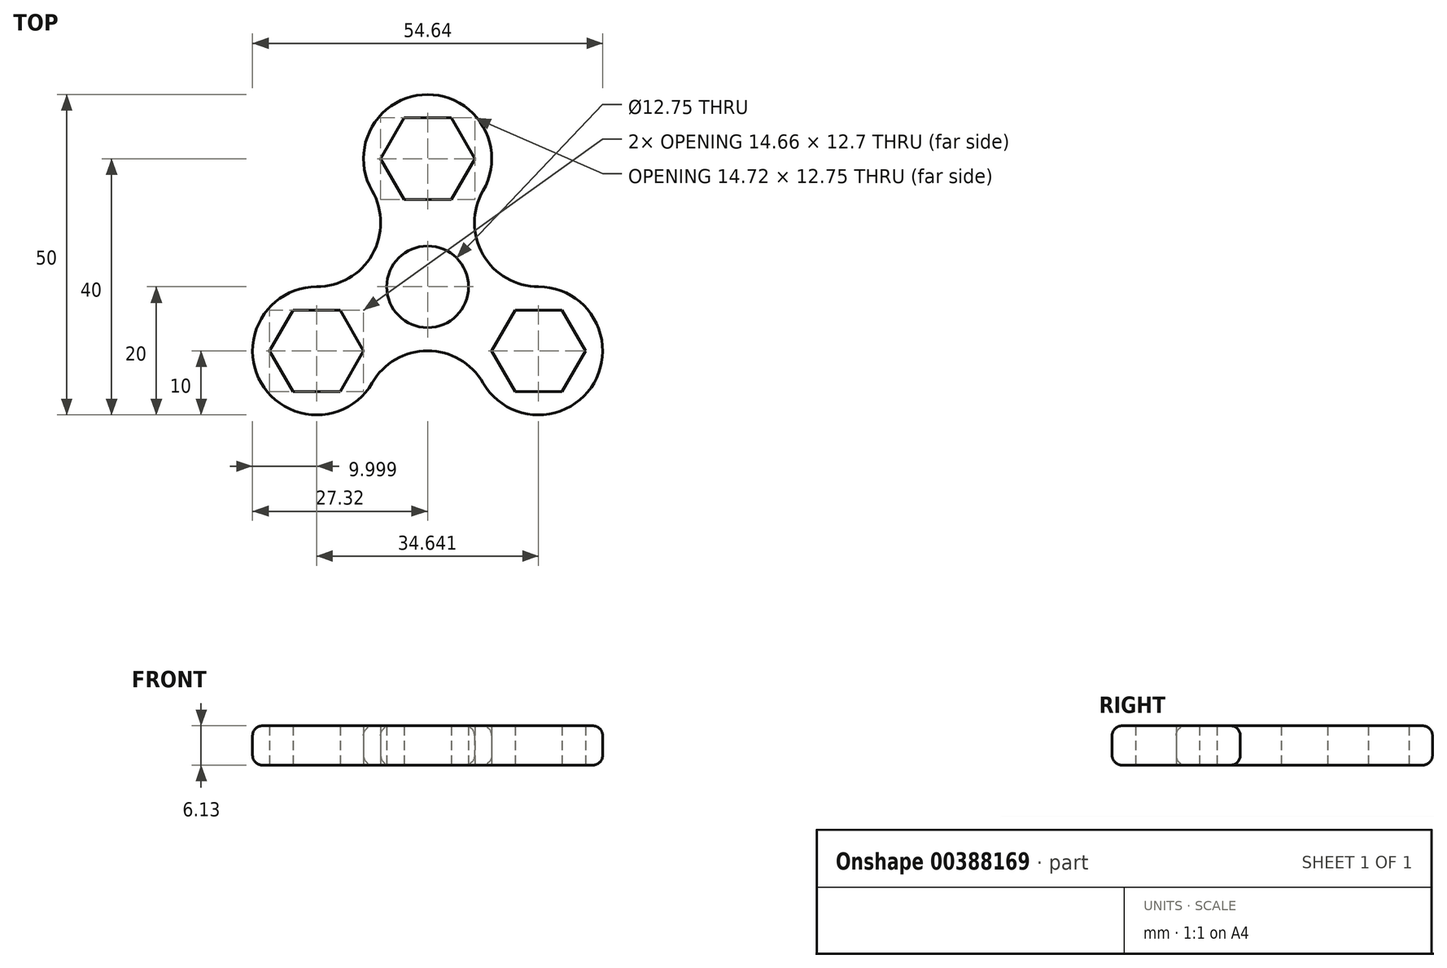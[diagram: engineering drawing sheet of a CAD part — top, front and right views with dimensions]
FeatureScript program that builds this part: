
annotation { "Feature Type Name" : "Feature", "Feature Type Description" : "" }
export const myFeature = defineFeature(function(context is Context, id is Id, definition is map)
    precondition{}
    {
        {
            var Q0;
            Q0=qCreatedBy(makeId("Top.planeOp"),FACE);
            var sketch = newSketch(context, id + "F0", { "sketchPlane" : qUnion([Q0])});
            skCircle(sketch, "E0", {"center": v(0, -20) * mm, "radius": 6.38 * mm});
            skLineSegment(sketch, "E1.0", {"start": v(-13.65, -23.65) * mm, "end": v(-9.99, -30) * mm});
            skLineSegment(sketch, "E1.1", {"start": v(-9.99, -30) * mm, "end": v(-13.65, -36.35) * mm});
            skLineSegment(sketch, "E1.2", {"start": v(-13.65, -36.35) * mm, "end": v(-20.99, -36.35) * mm});
            skLineSegment(sketch, "E1.3", {"start": v(-20.99, -36.35) * mm, "end": v(-24.65, -30) * mm});
            skLineSegment(sketch, "E1.4", {"start": v(-24.65, -30) * mm, "end": v(-20.99, -23.65) * mm});
            skLineSegment(sketch, "E1.5", {"start": v(-20.99, -23.65) * mm, "end": v(-13.65, -23.65) * mm});
            skPoint(sketch, "E1.0.midPoint", {"position": v(-11.82, -26.83) * mm});
            skLineSegment(sketch, "E2.0", {"start": v(9.99, -30) * mm, "end": v(13.65, -23.65) * mm});
            skLineSegment(sketch, "E2.1", {"start": v(13.65, -23.65) * mm, "end": v(20.99, -23.65) * mm});
            skLineSegment(sketch, "E2.2", {"start": v(20.99, -23.65) * mm, "end": v(24.65, -30) * mm});
            skLineSegment(sketch, "E2.3", {"start": v(24.65, -30) * mm, "end": v(20.99, -36.35) * mm});
            skLineSegment(sketch, "E2.4", {"start": v(20.99, -36.35) * mm, "end": v(13.65, -36.35) * mm});
            skLineSegment(sketch, "E2.5", {"start": v(13.65, -36.35) * mm, "end": v(9.99, -30) * mm});
            skPoint(sketch, "E2.0.midPoint", {"position": v(11.82, -26.83) * mm});
            skLineSegment(sketch, "E3.0", {"start": v(3.68, -6.38) * mm, "end": v(-3.68, -6.38) * mm});
            skLineSegment(sketch, "E3.1", {"start": v(-3.68, -6.38) * mm, "end": v(-7.36, 0) * mm});
            skLineSegment(sketch, "E3.2", {"start": v(-7.36, 0) * mm, "end": v(-3.68, 6.37) * mm});
            skLineSegment(sketch, "E3.3", {"start": v(-3.68, 6.37) * mm, "end": v(3.68, 6.38) * mm});
            skLineSegment(sketch, "E3.4", {"start": v(3.68, 6.38) * mm, "end": v(7.36, 0) * mm});
            skLineSegment(sketch, "E3.5", {"start": v(7.36, 0) * mm, "end": v(3.68, -6.38) * mm});
            skPoint(sketch, "E3.0.midPoint", {"position": v(0, -6.38) * mm});
            skPoint(sketch, "E4.endSnap0", {"position": v(17.32, -23.65) * mm});
            skPoint(sketch, "E5.endSnap0", {"position": v(-17.32, -23.65) * mm});
            skArc(sketch, "E6", {"start": v(8.66, -5) * mm, "mid": v(8.66, -15) * mm, "end": v(17.32, -20) * mm});
            skArc(sketch, "E7", {"start": v(8.66, -35) * mm, "mid": v(0, -30) * mm, "end": v(-8.66, -35) * mm});
            skArc(sketch, "E8", {"start": v(-17.32, -20) * mm, "mid": v(-8.66, -15) * mm, "end": v(-8.66, -5) * mm});
            skLineSegment(sketch, "E9", {"start": v(17.32, -30) * mm, "end": v(25.98, -35) * mm});
            skLineSegment(sketch, "E10", {"start": v(0, 0) * mm, "end": v(0, 10) * mm});
            skPoint(sketch, "E10.endSnap0", {"position": v(0, 6.38) * mm});
            skLineSegment(sketch, "E11", {"start": v(-17.32, -30) * mm, "end": v(-25.98, -35) * mm});
            skArc(sketch, "E12", {"start": v(-17.32, -20) * mm, "mid": v(-25.98, -35) * mm, "end": v(-8.66, -35) * mm});
            skArc(sketch, "E13", {"start": v(8.66, -35) * mm, "mid": v(25.98, -35) * mm, "end": v(17.32, -20) * mm});
            skArc(sketch, "E14", {"start": v(8.66, -5) * mm, "mid": v(0, 10) * mm, "end": v(-8.66, -5) * mm});
            skSolve(sketch);
        }
        {
            var Q0;
            Q0=makeQuery(id+"F0.imprint","IMPRINT",FACE,{"disambiguationData":[TD([[makeQuery(id+"F0.imprint","IMPRINT",EDGE,{"derivedFrom":sQuery(id+"F0.wireOp",EDGE,"E0")}),-1.0]])]});
            extrude(context, id + "F1", {"entities" : qUnion([Q0]), "depth" : 6.12 * mm, "offsetDistance" : 25 * mm});
        }
        {
            var Q0;
            Q0=makeQuery(id+"F1.opExtrude","CAP_EDGE",EDGE,{"disambiguationData":[OSD([sQuery(id+"F0.wireOp",EDGE,"E8")])],"isStart":false});
            var Q1;
            Q1=makeQuery(id+"F1.opExtrude","CAP_EDGE",EDGE,{"disambiguationData":[OSD([sQuery(id+"F0.wireOp",EDGE,"E8")])],"isStart":true});
            fillet(context, id + "F2", {"entities" : qUnion([Q0, Q1]), "radius" : 1.5 * mm, "tangentPropagation" : true, "allowEdgeOverflow" : false});
        }
    });
